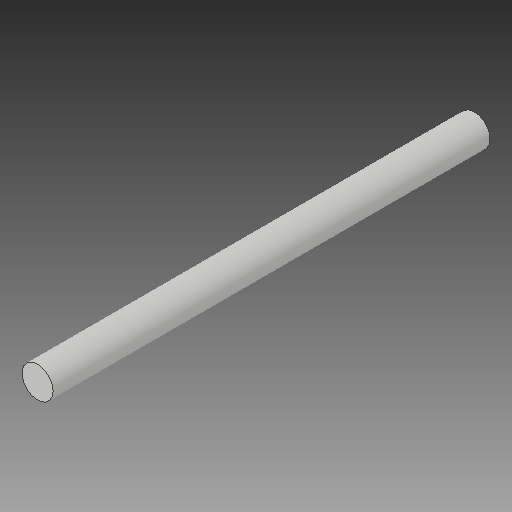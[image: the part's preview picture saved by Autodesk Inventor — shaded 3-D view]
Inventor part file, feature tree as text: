
AUTODESK INVENTOR PART (.ipt)
format: ipt  version: 2017 (Build 210142000, 142)  size: 87,040 bytes
history: native  units: in
note: dims shown in document units (in); Inventor stores cm internally (conversion verified against a paired STEP export)
features: extrude x1, sketch x1
ambient origin geometry x8: Origin, YZ Plane, XZ Plane, XY Plane, X Axis, Y Axis, Z Axis, Center Point
bodies: Solid1 (feature_tree)
feature tree (2):
  extrude  "Extrusion1"  Depth=1.5in TaperAngle=0.0deg
  sketch  "Sketch1"  dims[d0=0.107in d1=1.5in d2=0.0in]
